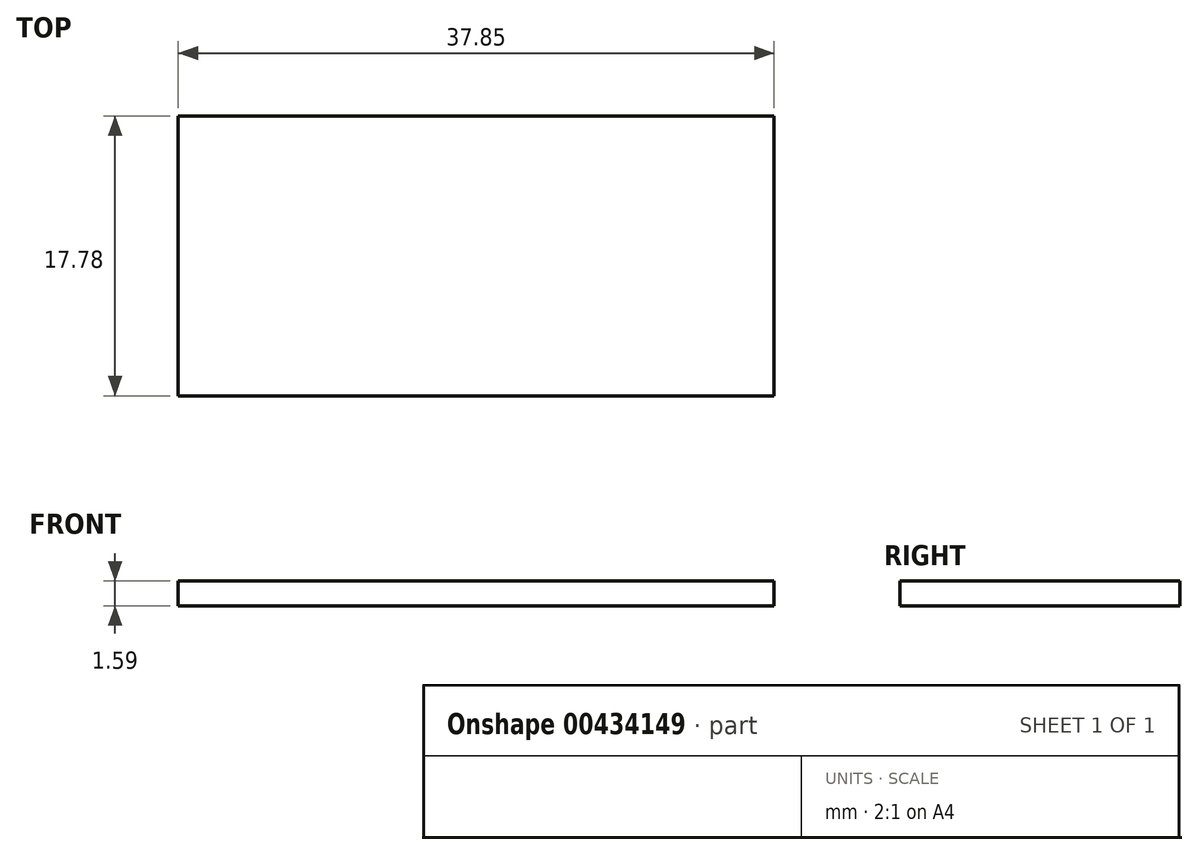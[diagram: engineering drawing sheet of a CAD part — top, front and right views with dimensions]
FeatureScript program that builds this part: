
annotation { "Feature Type Name" : "Feature", "Feature Type Description" : "" }
export const myFeature = defineFeature(function(context is Context, id is Id, definition is map)
    precondition{}
    {
        {
            var Q0;
            Q0=qCreatedBy(makeId("Top.planeOp"),FACE);
            var sketch = newSketch(context, id + "F0", { "sketchPlane" : qUnion([Q0])});
            skLineSegment(sketch, "E0.bottom", {"start": v(0, 0) * mm, "end": v(-37.85, 0) * mm});
            skLineSegment(sketch, "E0.top", {"start": v(0, 17.78) * mm, "end": v(-37.85, 17.78) * mm});
            skLineSegment(sketch, "E0.left", {"start": v(0, 0) * mm, "end": v(0, 17.78) * mm});
            skLineSegment(sketch, "E0.right", {"start": v(-37.85, 0) * mm, "end": v(-37.85, 17.78) * mm});
            skSolve(sketch);
        }
        {
            var Q0;
            Q0=makeQuery(id+"F0.imprint","IMPRINT",FACE,{"disambiguationData":[TD([[makeQuery(id+"F0.imprint","IMPRINT",EDGE,{"derivedFrom":sQuery(id+"F0.wireOp",EDGE,"E0.bottom")}),-1.0]])]});
            extrude(context, id + "F1", {"entities" : qUnion([Q0]), "depth" : 1.59 * mm});
        }
        {
            var Q0;
            Q0=makeQuery(id+"F1.opExtrude","SWEPT_FACE",FACE,{"disambiguationData":[OSD([sQuery(id+"F0.wireOp",EDGE,"E0.left")])]});
            cPlane(context, id + "F2", {"entities" : qUnion([Q0]), "cplaneType" : CPlaneType.OFFSET, "offset" : 25.4 * mm, "width" : 152.4 * mm, "height" : 152.4 * mm});
        }
    });
